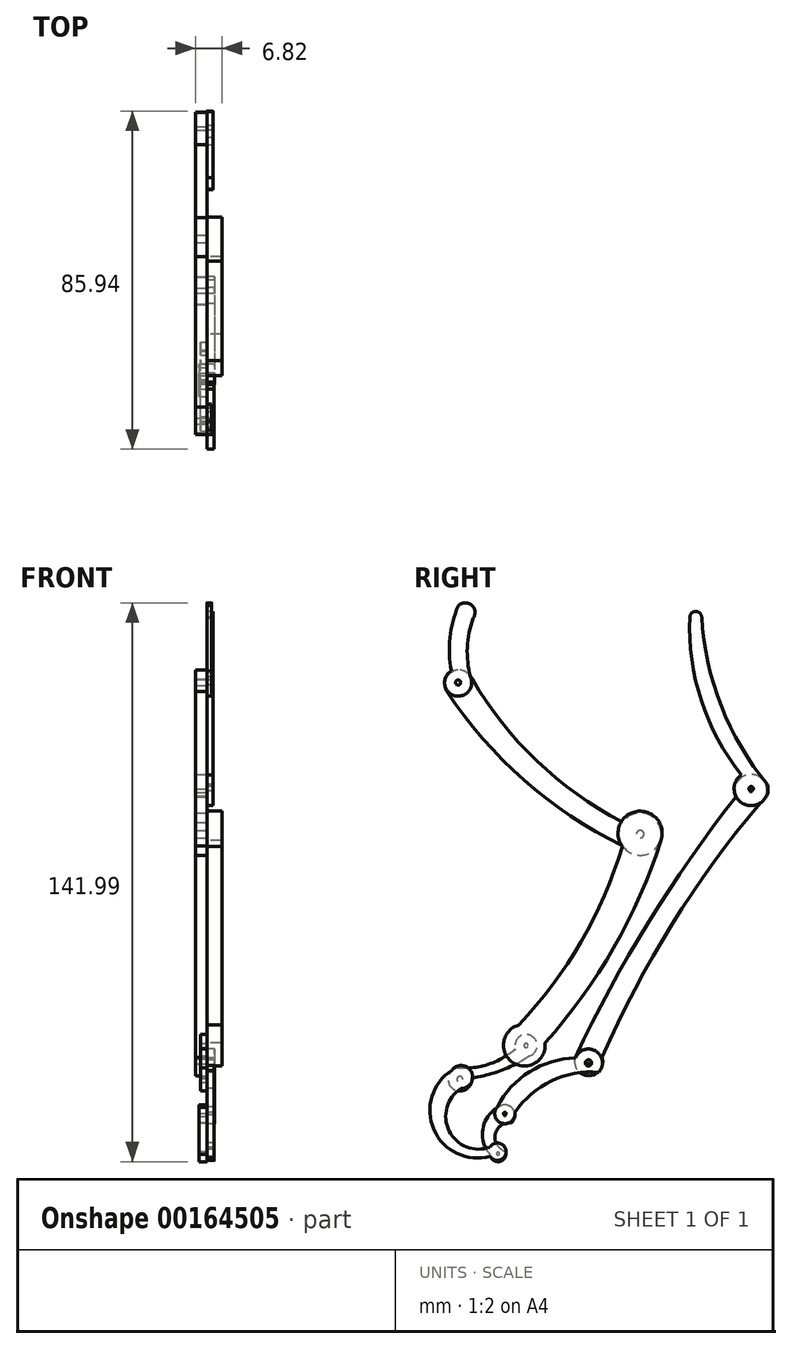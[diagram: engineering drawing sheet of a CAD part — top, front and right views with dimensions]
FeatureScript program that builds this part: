
annotation { "Feature Type Name" : "Feature", "Feature Type Description" : "" }
export const myFeature = defineFeature(function(context is Context, id is Id, definition is map)
    precondition{}
    {
        {
            var Q0;
            Q0=qCreatedBy(makeId("Right.planeOp"),FACE);
            var sketch = newSketch(context, id + "F10", { "sketchPlane" : qUnion([Q0])});
            skArc(sketch, "E0", {"start": v(-58.83, 27.15) * mm, "mid": v(-60.94, 19.01) * mm, "end": v(-60.57, 10.62) * mm});
            skArc(sketch, "E1", {"start": v(-55.05, 23.91) * mm, "mid": v(-56.53, 16.53) * mm, "end": v(-55.72, 9.05) * mm});
            skArc(sketch, "E2", {"start": v(-60.57, 10.62) * mm, "mid": v(-59.93, 4.33) * mm, "end": v(-55.72, 9.05) * mm});
            skArc(sketch, "E3", {"start": v(-55.05, 23.91) * mm, "mid": v(-55.44, 27.28) * mm, "end": v(-58.83, 27.15) * mm});
            skCircle(sketch, "E4", {"center": v(-58.86, 7.62) * mm, "radius": 0.65 * mm});
            skSolve(sketch);
        }
        {
            var Q0;
            Q0=makeQuery(id+"F10.imprint","IMPRINT",FACE,{"disambiguationData":[TD([[makeQuery(id+"F10.imprint","IMPRINT",EDGE,{"derivedFrom":sQuery(id+"F10.wireOp",EDGE,"E0")}),1.0]])]});
            extrude(context, id + "F11", {"entities" : qUnion([Q0]), "depth" : 1.18 * mm});
        }
        {
            var Q0;
            Q0=qCreatedBy(makeId("Right.planeOp"),FACE);
            var sketch = newSketch(context, id + "F12", { "sketchPlane" : qUnion([Q0])});
            skCircle(sketch, "E5", {"center": v(-58.86, 7.62) * mm, "radius": 0.72 * mm});
            skArc(sketch, "E6", {"start": v(-55.28, 8.47) * mm, "mid": v(-60.19, 10.46) * mm, "end": v(-61.76, 5.4) * mm});
            skArc(sketch, "E7", {"start": v(-61.76, 5.4) * mm, "mid": v(-42.04, -17.21) * mm, "end": v(-17.07, -33.87) * mm});
            skArc(sketch, "E8", {"start": v(-55.28, 8.47) * mm, "mid": v(-38.74, -12.41) * mm, "end": v(-17.07, -27.9) * mm});
            skArc(sketch, "E9", {"start": v(-17.07, -33.87) * mm, "mid": v(-7.24, -30.9) * mm, "end": v(-17.07, -27.9) * mm});
            skCircle(sketch, "E10", {"center": v(-12.6, -30.9) * mm, "radius": 0.96 * mm});
            skSolve(sketch);
        }
        {
            var Q0;
            Q0=makeQuery(id+"F12.imprint","IMPRINT",FACE,{"disambiguationData":[TD([[makeQuery(id+"F12.imprint","IMPRINT",EDGE,{"derivedFrom":sQuery(id+"F12.wireOp",EDGE,"E5")}),-1.0]])]});
            extrude(context, id + "F0", {"entities" : qUnion([Q0]), "operationType" : NewBodyOperationType.ADD, "oppositeDirection" : true, "depth" : 2.9 * mm});
        }
        {
            var Q0;
            Q0=qCreatedBy(makeId("Right.planeOp"),FACE);
            var sketch = newSketch(context, id + "F1", { "sketchPlane" : qUnion([Q0])});
            skArc(sketch, "E11", {"start": v(-36.77, -83.97) * mm, "mid": v(-19.34, -59.77) * mm, "end": v(-7.32, -32.48) * mm});
            skArc(sketch, "E12", {"start": v(-43.46, -79.4) * mm, "mid": v(-27.65, -58.24) * mm, "end": v(-17.13, -34) * mm});
            skArc(sketch, "E13", {"start": v(-7.32, -32.48) * mm, "mid": v(-13.5, -25.12) * mm, "end": v(-17.13, -34) * mm});
            skArc(sketch, "E14", {"start": v(-43.46, -79.4) * mm, "mid": v(-45.03, -88.9) * mm, "end": v(-36.77, -83.97) * mm});
            skSolve(sketch);
        }
        {
            var Q0;
            Q0=makeQuery(id+"F1.imprint","IMPRINT",FACE,{"disambiguationData":[TD([[makeQuery(id+"F1.imprint","IMPRINT",EDGE,{"derivedFrom":sQuery(id+"F1.wireOp",EDGE,"E11")}),1.0]])]});
            var sketch = newSketch(context, id + "F2", { "sketchPlane" : qUnion([Q0])});
            skCircle(sketch, "E15", {"center": v(-42.04, -84.3) * mm, "radius": 1.6 * mm});
            skSolve(sketch);
        }
        {
            var Q0;
            Q0=makeQuery(id+"F1.imprint","IMPRINT",FACE,{"disambiguationData":[TD([[makeQuery(id+"F1.imprint","IMPRINT",EDGE,{"derivedFrom":sQuery(id+"F1.wireOp",EDGE,"E11")}),1.0]])]});
            var Q1;
            Q1=makeQuery(id+"F2.imprint","IMPRINT",FACE,{"disambiguationData":[TD([[makeQuery(id+"F2.imprint","IMPRINT",EDGE,{"derivedFrom":sQuery(id+"F2.wireOp",EDGE,"E15")}),1.0]])]});
            extrude(context, id + "F13", {"entities" : qUnion([Q0, Q1]), "operationType" : NewBodyOperationType.ADD, "depth" : 3.85 * mm});
        }
        {
            var Q0;
            Q0=qCreatedBy(makeId("Right.planeOp"),FACE);
            var sketch = newSketch(context, id + "F14", { "sketchPlane" : qUnion([Q0])});
            skArc(sketch, "E16", {"start": v(0, 24.22) * mm, "mid": v(2.9, 3.01) * mm, "end": v(13.1, -15.8) * mm});
            skArc(sketch, "E17", {"start": v(3.02, 24.22) * mm, "mid": v(8, 1.61) * mm, "end": v(19.76, -18.32) * mm});
            skArc(sketch, "E18", {"start": v(13.1, -15.8) * mm, "mid": v(14.05, -23.39) * mm, "end": v(19.76, -18.32) * mm});
            skArc(sketch, "E19", {"start": v(3.02, 24.22) * mm, "mid": v(1.5, 25.69) * mm, "end": v(0, 24.22) * mm});
            skCircle(sketch, "E20", {"center": v(15.57, -19.35) * mm, "radius": 0.56 * mm});
            skSolve(sketch);
        }
        {
            var Q0;
            Q0=makeQuery(id+"F14.imprint","IMPRINT",FACE,{"disambiguationData":[TD([[makeQuery(id+"F14.imprint","IMPRINT",EDGE,{"derivedFrom":sQuery(id+"F14.wireOp",EDGE,"E16")}),1.0]])]});
            extrude(context, id + "F15", {"entities" : qUnion([Q0]), "depth" : 1.5 * mm});
        }
        {
            var Q0;
            Q0=qCreatedBy(makeId("Right.planeOp"),FACE);
            var sketch = newSketch(context, id + "F3", { "sketchPlane" : qUnion([Q0])});
            skArc(sketch, "E21", {"start": v(19.4, -21.22) * mm, "mid": v(-3.9, -52.85) * mm, "end": v(-22.3, -87.56) * mm});
            skArc(sketch, "E22", {"start": v(11.67, -21.43) * mm, "mid": v(-10.55, -53.36) * mm, "end": v(-29.1, -87.56) * mm});
            skArc(sketch, "E23", {"start": v(19.4, -21.22) * mm, "mid": v(15.38, -15.72) * mm, "end": v(11.67, -21.43) * mm});
            skArc(sketch, "E24", {"start": v(-29.1, -87.56) * mm, "mid": v(-25.7, -92.26) * mm, "end": v(-22.3, -87.56) * mm});
            skCircle(sketch, "E25", {"center": v(15.5, -19.86) * mm, "radius": 0.45 * mm});
            skCircle(sketch, "E26", {"center": v(-25.7, -88.67) * mm, "radius": 0.62 * mm});
            skSolve(sketch);
        }
        {
            var Q0;
            Q0=makeQuery(id+"F3.imprint","IMPRINT",FACE,{"disambiguationData":[TD([[makeQuery(id+"F3.imprint","IMPRINT",EDGE,{"derivedFrom":sQuery(id+"F3.wireOp",EDGE,"E21")}),-1.0]])]});
            extrude(context, id + "F4", {"entities" : qUnion([Q0]), "operationType" : NewBodyOperationType.ADD, "oppositeDirection" : true, "depth" : 2.97 * mm});
        }
        {
            var Q0;
            Q0=qCreatedBy(makeId("Right.planeOp"),FACE);
            var sketch = newSketch(context, id + "F16", { "sketchPlane" : qUnion([Q0])});
            skArc(sketch, "E27", {"start": v(-23.1, -91.39) * mm, "mid": v(-35.14, -93.61) * mm, "end": v(-44.44, -101.56) * mm});
            skArc(sketch, "E28", {"start": v(-29.04, -87.75) * mm, "mid": v(-40.69, -91.24) * mm, "end": v(-48.92, -100.19) * mm});
            skArc(sketch, "E29", {"start": v(-23.1, -91.39) * mm, "mid": v(-23.9, -86.02) * mm, "end": v(-29.04, -87.75) * mm});
            skArc(sketch, "E30", {"start": v(-48.92, -100.19) * mm, "mid": v(-47.74, -104.36) * mm, "end": v(-44.44, -101.56) * mm});
            skCircle(sketch, "E31", {"center": v(-25.74, -89.03) * mm, "radius": 0.8 * mm});
            skCircle(sketch, "E32", {"center": v(-47, -101.9) * mm, "radius": 0.35 * mm});
            skSolve(sketch);
        }
        {
            var Q0;
            Q0=makeQuery(id+"F16.imprint","IMPRINT",FACE,{"disambiguationData":[TD([[makeQuery(id+"F16.imprint","IMPRINT",EDGE,{"derivedFrom":sQuery(id+"F16.wireOp",EDGE,"E27")}),-1.0]])]});
            extrude(context, id + "F5", {"entities" : qUnion([Q0]), "operationType" : NewBodyOperationType.ADD, "depth" : 1.91 * mm});
        }
        {
            var Q0;
            Q0=qCreatedBy(makeId("Right.planeOp"),FACE);
            var sketch = newSketch(context, id + "F6", { "sketchPlane" : qUnion([Q0])});
            skArc(sketch, "E33", {"start": v(-55.43, -92.9) * mm, "mid": v(-47.82, -90.86) * mm, "end": v(-40.8, -87.27) * mm});
            skArc(sketch, "E34", {"start": v(-58.87, -90.22) * mm, "mid": v(-51.06, -89.35) * mm, "end": v(-44.27, -85.4) * mm});
            skArc(sketch, "E35", {"start": v(-40.8, -87.27) * mm, "mid": v(-40.27, -82.13) * mm, "end": v(-44.27, -85.4) * mm});
            skArc(sketch, "E36", {"start": v(-58.87, -90.22) * mm, "mid": v(-60.25, -95.54) * mm, "end": v(-55.43, -92.9) * mm});
            skCircle(sketch, "E37", {"center": v(-41.6, -84.6) * mm, "radius": 0.51 * mm});
            skCircle(sketch, "E38", {"center": v(-58.41, -93.18) * mm, "radius": 0.74 * mm});
            skSolve(sketch);
        }
        {
            var Q0;
            Q0=makeQuery(id+"F6.imprint","IMPRINT",FACE,{"disambiguationData":[TD([[makeQuery(id+"F6.imprint","IMPRINT",EDGE,{"derivedFrom":sQuery(id+"F6.wireOp",EDGE,"E33")}),1.0]])]});
            extrude(context, id + "F17", {"entities" : qUnion([Q0]), "operationType" : NewBodyOperationType.ADD, "oppositeDirection" : true, "depth" : 1.68 * mm});
        }
        {
            var Q0;
            Q0=qCreatedBy(makeId("Right.planeOp"),FACE);
            var sketch = newSketch(context, id + "F7", { "sketchPlane" : qUnion([Q0])});
            skArc(sketch, "E39", {"start": v(-58.11, -95.52) * mm, "mid": v(-61.15, -106.28) * mm, "end": v(-50.76, -110.41) * mm});
            skArc(sketch, "E40", {"start": v(-60.44, -90.89) * mm, "mid": v(-65.01, -105.98) * mm, "end": v(-50.76, -112.74) * mm});
            skArc(sketch, "E41", {"start": v(-58.11, -95.52) * mm, "mid": v(-55.47, -91.3) * mm, "end": v(-60.44, -90.89) * mm});
            skArc(sketch, "E42", {"start": v(-50.76, -112.74) * mm, "mid": v(-46.68, -111.58) * mm, "end": v(-50.76, -110.41) * mm});
            skSolve(sketch);
        }
        {
            var Q0;
            Q0=makeQuery(id+"F7.imprint","IMPRINT",FACE,{"disambiguationData":[TD([[makeQuery(id+"F7.imprint","IMPRINT",EDGE,{"derivedFrom":sQuery(id+"F7.wireOp",EDGE,"E39")}),-1.0]])]});
            extrude(context, id + "F18", {"entities" : qUnion([Q0]), "operationType" : NewBodyOperationType.ADD, "depth" : 1.79 * mm});
        }
        {
            var Q0;
            Q0=qCreatedBy(makeId("Right.planeOp"),FACE);
            var sketch = newSketch(context, id + "F8", { "sketchPlane" : qUnion([Q0])});
            skArc(sketch, "E43", {"start": v(-45.33, -104.22) * mm, "mid": v(-49.46, -107.21) * mm, "end": v(-46.74, -111.53) * mm});
            skArc(sketch, "E44", {"start": v(-48.6, -100.26) * mm, "mid": v(-52.59, -105.76) * mm, "end": v(-50.76, -112.3) * mm});
            skArc(sketch, "E45", {"start": v(-45.33, -104.22) * mm, "mid": v(-45.02, -100.63) * mm, "end": v(-48.6, -100.26) * mm});
            skArc(sketch, "E46", {"start": v(-50.76, -112.3) * mm, "mid": v(-48.34, -114.07) * mm, "end": v(-46.74, -111.53) * mm});
            skCircle(sketch, "E47", {"center": v(-47, -102.26) * mm, "radius": 0.37 * mm});
            skCircle(sketch, "E48", {"center": v(-48.73, -112.05) * mm, "radius": 0.37 * mm});
            skSolve(sketch);
        }
        {
            var Q0;
            Q0=makeQuery(id+"F8.imprint","IMPRINT",FACE,{"disambiguationData":[TD([[makeQuery(id+"F8.imprint","IMPRINT",EDGE,{"derivedFrom":sQuery(id+"F8.wireOp",EDGE,"E43")}),-1.0]])]});
            extrude(context, id + "F9", {"entities" : qUnion([Q0]), "oppositeDirection" : true, "depth" : 2 * mm});
        }
    });
